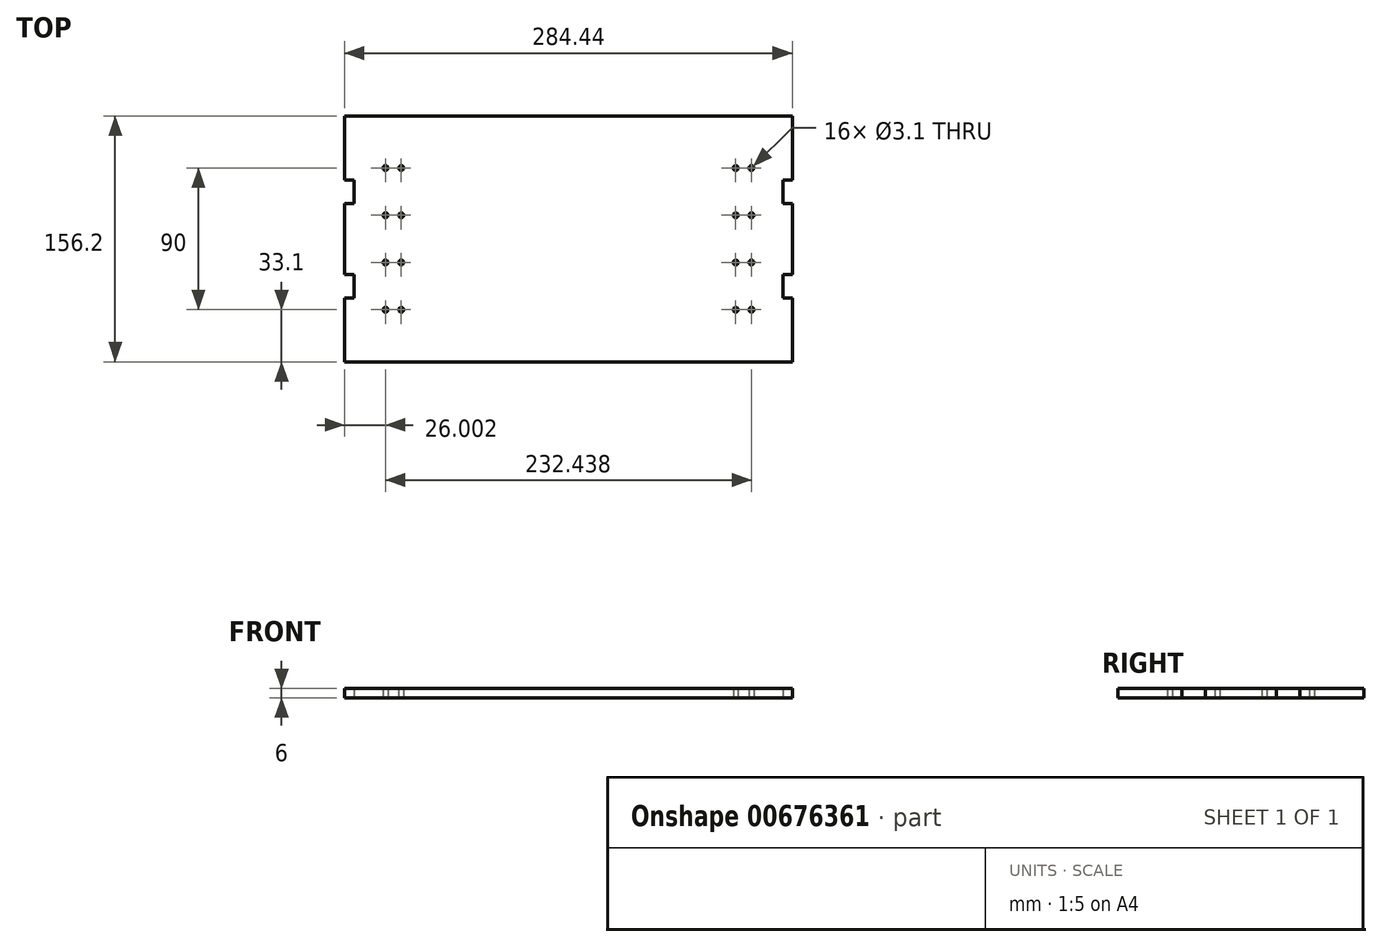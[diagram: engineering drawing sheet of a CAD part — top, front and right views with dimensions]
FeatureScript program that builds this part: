
annotation { "Feature Type Name" : "Feature", "Feature Type Description" : "" }
export const myFeature = defineFeature(function(context is Context, id is Id, definition is map)
    precondition{}
    {
        {
            var Q0;
            Q0=qCreatedBy(makeId("Top.planeOp"),FACE);
            var sketch = newSketch(context, id + "F0", { "sketchPlane" : qUnion([Q0])});
            skLineSegment(sketch, "E0.bottom", {"start": v(0, 0) * mm, "end": v(-284.44, 0) * mm});
            skLineSegment(sketch, "E0.top", {"start": v(0, 156.2) * mm, "end": v(-284.44, 156.2) * mm});
            skLineSegment(sketch, "E0.left", {"start": v(0, 0) * mm, "end": v(0, 156.2) * mm});
            skLineSegment(sketch, "E0.right", {"start": v(-284.44, 0) * mm, "end": v(-284.44, 156.2) * mm});
            skLineSegment(sketch, "E1", {"start": v(-284.44, 40.6) * mm, "end": v(-278.44, 40.6) * mm});
            skLineSegment(sketch, "E2", {"start": v(-278.44, 40.6) * mm, "end": v(-278.44, 55.6) * mm});
            skLineSegment(sketch, "E3", {"start": v(-278.44, 55.6) * mm, "end": v(-284.44, 55.6) * mm});
            skLineSegment(sketch, "E4", {"start": v(-284.44, 100.6) * mm, "end": v(-278.44, 100.6) * mm});
            skLineSegment(sketch, "E5", {"start": v(-278.44, 100.6) * mm, "end": v(-278.44, 115.6) * mm});
            skLineSegment(sketch, "E6", {"start": v(-278.44, 115.6) * mm, "end": v(-284.44, 115.6) * mm});
            skLineSegment(sketch, "E7", {"start": v(-142.22, 209.54) * mm, "end": v(-142.22, -21.9) * mm, "construction": true});
            skPoint(sketch, "E7.startSnap0", {"position": v(-142.22, 156.2) * mm});
            skLineSegment(sketch, "E8.MirrorCS", {"start": v(-6, 115.6) * mm, "end": v(0, 115.6) * mm});
            skLineSegment(sketch, "E9.MirrorCS", {"start": v(-6, 100.6) * mm, "end": v(-6, 115.6) * mm});
            skLineSegment(sketch, "E10.MirrorCS", {"start": v(0, 100.6) * mm, "end": v(-6, 100.6) * mm});
            skLineSegment(sketch, "E11.MirrorCS", {"start": v(-6, 55.6) * mm, "end": v(0, 55.6) * mm});
            skLineSegment(sketch, "E12.MirrorCS", {"start": v(0, 40.6) * mm, "end": v(-6, 40.6) * mm});
            skLineSegment(sketch, "E13.MirrorCS", {"start": v(-6, 40.6) * mm, "end": v(-6, 55.6) * mm});
            skPoint(sketch, "E14.centerSnap0", {"position": v(-278.44, 108.1) * mm});
            skPoint(sketch, "E15.centerSnap0", {"position": v(-278.44, 48.1) * mm});
            skCircle(sketch, "E16", {"center": v(-258.44, 123.1) * mm, "radius": 1.55 * mm});
            skCircle(sketch, "E17", {"center": v(-258.44, 93.1) * mm, "radius": 1.55 * mm});
            skCircle(sketch, "E18", {"center": v(-258.44, 63.1) * mm, "radius": 1.55 * mm});
            skCircle(sketch, "E19", {"center": v(-258.44, 33.1) * mm, "radius": 1.55 * mm});
            skCircle(sketch, "E20.MirrorC", {"center": v(-26, 123.1) * mm, "radius": 1.55 * mm});
            skCircle(sketch, "E21.MirrorC", {"center": v(-26, 93.1) * mm, "radius": 1.55 * mm});
            skCircle(sketch, "E22.MirrorC", {"center": v(-26, 33.1) * mm, "radius": 1.55 * mm});
            skCircle(sketch, "E23.MirrorC", {"center": v(-26, 63.1) * mm, "radius": 1.55 * mm});
            skCircle(sketch, "E24", {"center": v(-248.44, 123.1) * mm, "radius": 1.55 * mm});
            skCircle(sketch, "E25", {"center": v(-248.44, 93.1) * mm, "radius": 1.55 * mm});
            skCircle(sketch, "E26", {"center": v(-248.44, 63.1) * mm, "radius": 1.55 * mm});
            skCircle(sketch, "E27", {"center": v(-248.44, 33.1) * mm, "radius": 1.55 * mm});
            skCircle(sketch, "E28.MirrorC", {"center": v(-36, 123.1) * mm, "radius": 1.55 * mm});
            skCircle(sketch, "E29.MirrorC", {"center": v(-36, 93.1) * mm, "radius": 1.55 * mm});
            skCircle(sketch, "E30.MirrorC", {"center": v(-36, 63.1) * mm, "radius": 1.55 * mm});
            skCircle(sketch, "E31.MirrorC", {"center": v(-36, 33.1) * mm, "radius": 1.55 * mm});
            skSolve(sketch);
        }
        {
            var Q0;
            {var subQ3=sQuery(id+"F0.wireOp",EDGE,"E0.bottom");Q0=makeQuery(id+"F0.imprint","IMPRINT",FACE,{"disambiguationData":[TD([[makeQuery(id+"F0.imprint","IMPRINT",EDGE,{"derivedFrom":subQ3}),-1.0]])]});}
            extrude(context, id + "F1", {"entities" : qUnion([Q0]), "depth" : 6 * mm, "offsetDistance" : 25 * mm});
        }
    });
